# Revit family: Hydrant-Ground_Zurn-Z1365-Encased_Flush Type_Non-Freeze
name_source: partatom
category: Plumbing Fixtures
units: mm (PartAtom-declared; Revit-internal decimal feet)

## family parameters
Cut with Voids When Loaded = No
Host = Face
Maintain Annotation Orientation = No
OmniClass Number = 23.65.70.00
OmniClass Title = Terminals for Supplied Liquids and Gases
Part Type = Normal
Room Calculation Point = No
Round Connector Dimension = Use Radius
Shared = No

## types (15) — shared parameters
Assembly Code = D2020100
Box and Cover = Iron - Zurn - Cast - Painted - Blue
CW Connection = Yes
CWFU = 1
Default Elevation = 48 "
Description = Ground Hydrant Encased, Flush Type, Non-Freeze
HW Connection = No
Hydrant Casing = Steel - Zurn - Galvanized
Manufacturer = Zurn Water, LLC
Manufacturer Brand = Zurn
Model = Z1365
Modified Date = 11/14/2025
Product Documentation Link = https://www.zurn.com
Product Installation Sheet URL = https://files.zurn.com
Product Page URL = https://www.zurn.com
Product data url = https://bimobject.com
URL = www.zurn.com
Vent Connection = No
Waste Connection = No
zero-valued in all types: HWFU, WFU

## per-type parameters (varying)
| type | Approx. Wt. | Depth Of Bury | Nominal Dia of Female I.P.S. | Nominal Dia of Hose Connection | Nominal Radius of Female I.P.S. | Nominal Radius of Hose Connection | Type Comments |
| Z1365 - 2' Depth of Bury w/2" Hose Connection | 42 " | 24 " | 2 " | 2 " | 1 " | 1 " | Z1365 - 2 Feet Depth of Bury with 2 Inch Hose Connection |
| Z1365 - 6' Depth of Bury w/2" Hose Connection | 58 " | 72 " | 2 " | 2 " | 1 " | 1 " | Z1365 - 6 Feet Depth of Bury with 2 Inch Hose Connection |
| Z1365 - 5' Depth of Bury w/2" Hose Connection | 54 " | 60 " | 2 " | 2 " | 1 " | 1 " | Z1365 - 5 Feet Depth of Bury with 2 Inch Hose Connection |
| Z1365 - 4' Depth of Bury w/2" Hose Connection | 50 " | 48 " | 2 " | 2 " | 1 " | 1 " | Z1365 - 4 Feet Depth of Bury with 2 Inch Hose Connection |
| Z1365 - 3' Depth of Bury w/2" Hose Connection | 46 " | 36 " | 2 " | 2 " | 1 " | 1 " | Z1365 - 3 Feet Depth of Bury with 2 Inch Hose Connection |
| Z1365 - 6' Depth of Bury w/1 1/4" Hose Connection | 58 " | 72 " | 1.25 " | 1.25 " | 0.625 " | 0.625 " | Z1365 - 6 Feet Depth of Bury with 1 1/4 Inch Hose Connection |
| Z1365 - 5' Depth of Bury w/1 1/4" Hose Connection | 54 " | 60 " | 1.25 " | 1.25 " | 0.625 " | 0.625 " | Z1365 - 5 Feet Depth of Bury with 1 1/4 Inch Hose Connection |
| Z1365 - 4' Depth of Bury w/1 1/4" Hose Connection | 50 " | 48 " | 1.25 " | 1.25 " | 0.625 " | 0.625 " | Z1365 - 4 Feet Depth of Bury with 1 1/4 Inch Hose Connection |
| Z1365 - 3' Depth of Bury w/1 1/4" Hose Connection | 46 " | 36 " | 1.25 " | 1.25 " | 0.625 " | 0.625 " | Z1365 - 3 Feet Depth of Bury with 1 1/4 Inch Hose Connection |
| Z1365 - 2' Depth of Bury w/1 1/4" Hose Connection | 42 " | 24 " | 1.25 " | 1.25 " | 0.625 " | 0.625 " | Z1365 - 3 Feet Depth of Bury with 1 1/4 Inch Hose Connection |
| Z1365 - 6' Depth of Bury w/1 1/2" Hose Connection | 58 " | 72 " | 1.5 " | 1.5 " | 0.75 " | 0.75 " | Z1365 - 6 Feet Depth of Bury with 1 1/2 Inch Hose Connection |
| Z1365 - 5' Depth of Bury w/1 1/2" Hose Connection | 54 " | 60 " | 1.5 " | 1.5 " | 0.75 " | 0.75 " | Z1365 - 3 Feet Depth of Bury with 1 1/2 Inch Hose Connection |
| Z1365 - 4' Depth of Bury w/1 1/2" Hose Connection | 50 " | 48 " | 1.5 " | 1.5 " | 0.75 " | 0.75 " | Z1365 - 4 Feet Depth of Bury with 1 1/2 Inch Hose Connection |
| Z1365 - 3' Depth of Bury w/1 1/2" Hose Connection | 46 " | 36 " | 1.5 " | 1.5 " | 0.75 " | 0.75 " | Z1365 - 3 Feet Depth of Bury with 1 1/2 Inch Hose Connection |
| Z1365 - 2' Depth of Bury w/1 1/2" Hose Connection | 42 " | 24 " | 1.5 " | 1.5 " | 0.75 " | 0.75 " | Z1365 - 3 Feet Depth of Bury with 1 1/2 Inch Hose Connection |

## geometry (parser evidence)
native form markers: Sweep x8
no freeform markers — native parametric forms only
